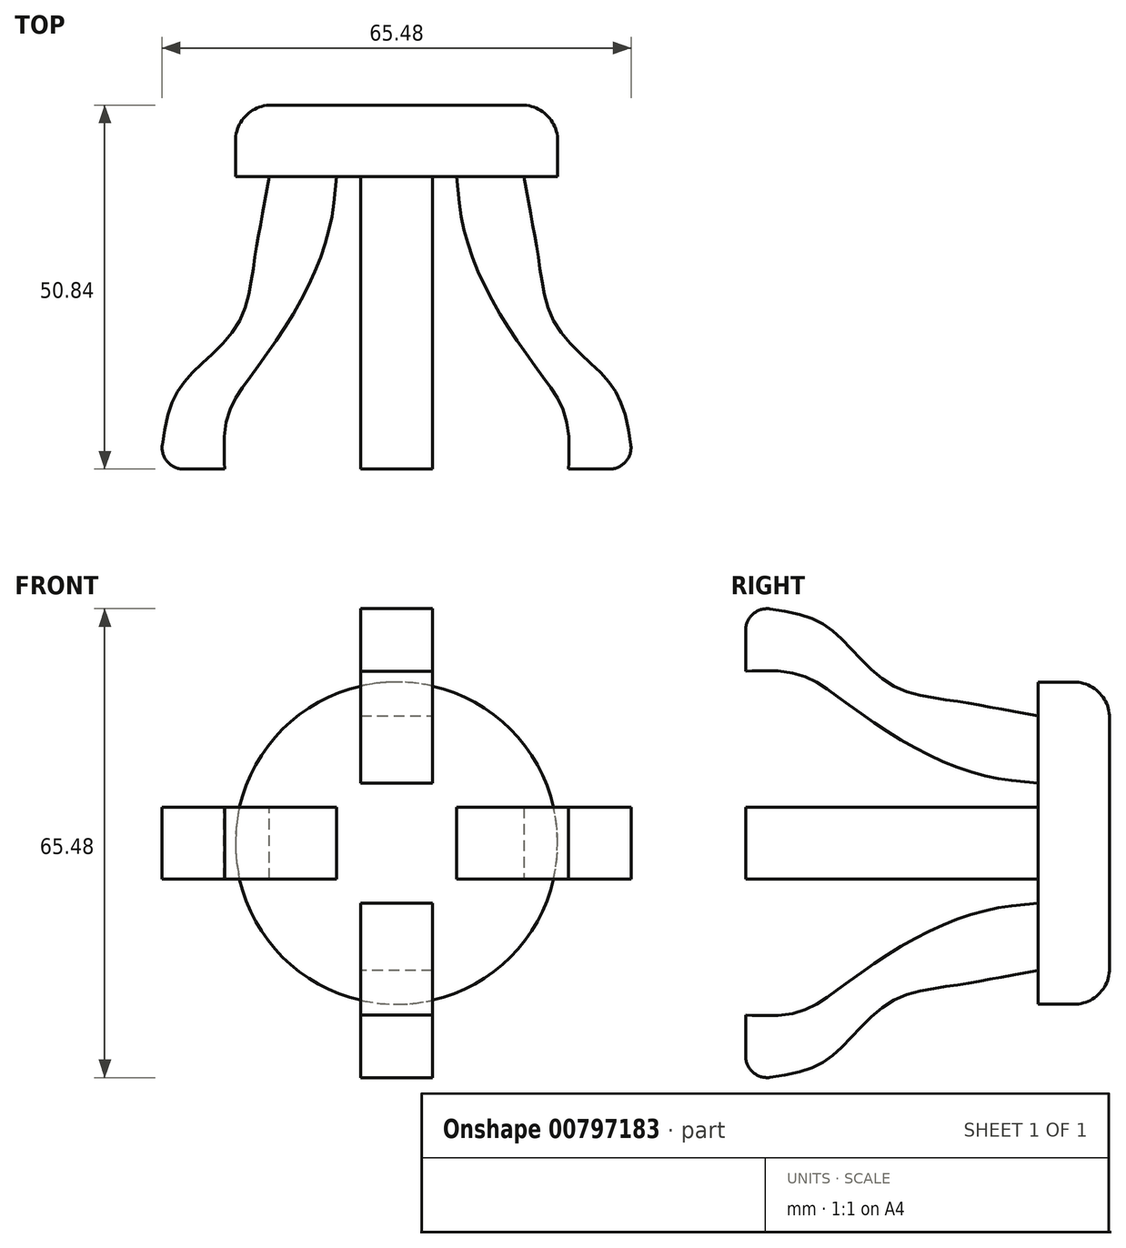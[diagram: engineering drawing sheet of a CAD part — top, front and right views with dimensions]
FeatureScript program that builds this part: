
annotation { "Feature Type Name" : "Feature", "Feature Type Description" : "" }
export const myFeature = defineFeature(function(context is Context, id is Id, definition is map)
    precondition{}
    {
        {
            var Q0;
            Q0=qCreatedBy(makeId("Front.planeOp"),FACE);
            var sketch = newSketch(context, id + "F0", { "sketchPlane" : qUnion([Q0])});
            skCircle(sketch, "E0", {"center": v(0, 0) * mm, "radius": 22.5 * mm});
            skSolve(sketch);
        }
        {
            var Q0;
            Q0 = qSketchRegion(id + "F0", true);
            extrude(context, id + "F1", {"entities" : qUnion([Q0]), "oppositeDirection" : true, "depth" : 10 * mm, "offsetDistance" : 25 * mm});
        }
        {
            var Q0;
            Q0=makeQuery(id+"F1.opExtrude","CAP_EDGE",EDGE,{"disambiguationData":[OSD([sQuery(id+"F0.wireOp",EDGE,"E0")])],"isStart":false});
            fillet(context, id + "F2", {"entities" : qUnion([Q0]), "radius" : 5 * mm, "tangentPropagation" : true, "allowEdgeOverflow" : false});
        }
        {
            var Q0;
            Q0=qCreatedBy(makeId("Top.planeOp"),FACE);
            var sketch = newSketch(context, id + "F3", { "sketchPlane" : qUnion([Q0])});
            skFitSpline(sketch, "E1", {"points": [v(17.76, 0) * mm, v(19.03, -6.84) * mm, v(19.98, -12.55) * mm, v(22.2, -20.63) * mm, v(28.54, -27.44) * mm, v(32.03, -33.62) * mm, v(33.04, -40.84) * mm, v(33.04, -41.03) * mm], "startDerivative": vector(8.45, -45.2) * mm, "endDerivative": vector(-0.27, -4.24) * mm});
            skFitSpline(sketch, "E2", {"points": [v(8.36, 0) * mm, v(9.68, -8.43) * mm, v(14.01, -18.42) * mm, v(20.23, -27.65) * mm, v(23.81, -34.43) * mm, v(24, -40.84) * mm, v(24, -41) * mm], "startDerivative": vector(4.2, -43.37) * mm, "endDerivative": vector(0.22, -3.45) * mm});
            skLineSegment(sketch, "E3", {"start": v(24, -40.84) * mm, "end": v(33.04, -40.84) * mm});
            skLineSegment(sketch, "E4", {"start": v(8.36, 0) * mm, "end": v(17.76, 0) * mm});
            skSolve(sketch);
        }
        {
            var Q0;
            Q0 = qSketchRegion(id + "F3", true);
            extrude(context, id + "F4", {"entities" : qUnion([Q0]), "operationType" : NewBodyOperationType.ADD, "endBound" : BoundingType.SYMMETRIC, "depth" : 10 * mm, "offsetDistance" : 25 * mm});
        }
        {
            var Q0;
            Q0=makeQuery(id+"F4.opExtrude","SWEPT_EDGE",EDGE,{"disambiguationData":[OSD([sQuery(id+"F3.wireOp",EDGE,"E1"),sQuery(id+"F3.wireOp",EDGE,"E3")])]});
            fillet(context, id + "F5", {"entities" : qUnion([Q0]), "radius" : 3 * mm, "tangentPropagation" : true, "allowEdgeOverflow" : false});
        }
        {
            var Q0;
            Q0=qCreatedBy(makeId("Top.planeOp"),FACE);
            var sketch = newSketch(context, id + "F6", { "sketchPlane" : qUnion([Q0])});
            skLineSegment(sketch, "E5", {"start": v(0, 31.37) * mm, "end": v(0, -51.34) * mm});
            skSolve(sketch);
        }
        {
            var Q0;
            Q0=makeQuery(id+"F1.opExtrude","SWEPT_BODY",BODY,{"disambiguationData":[OSD([sQuery(id+"F0.wireOp",EDGE,"E0")])]});
            var Q1;
            Q1=sQuery(id+"F6.wireOp",EDGE,"E5");
            circularPattern(context, id + "F7", {"entities" : qUnion([Q0]), "axis" : qUnion([Q1]), "angle" : 360 * degree, "instanceCount" : 4, "equalSpace" : true});
        }
    });
